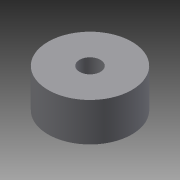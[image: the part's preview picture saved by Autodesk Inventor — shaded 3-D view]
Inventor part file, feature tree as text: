
AUTODESK INVENTOR PART (.ipt)
format: ipt  version: 2014 SP1 (Build 180222100, 222)  size: 84,480 bytes
history: native  units: in
note: dims shown in document units (in); Inventor stores cm internally (conversion verified against a paired STEP export)
features: extrude x2, sketch x2, hole x1
ambient origin geometry x8: Origin, YZ Plane, XZ Plane, XY Plane, X Axis, Y Axis, Z Axis, Center Point
bodies: Solid1 (feature_tree)
feature tree (5):
  extrude  "Extrusion1"  Depth=0.04in TaperAngle=0.0deg
  extrude  "Extrusion2"  Depth=0.46in TaperAngle=0.0deg
  hole  "Hole1"  [1 undecoded]
  sketch  "Sketch1"  dims[d0=0.75in d1=0.04in d2=0.0in]
  sketch  "Sketch2"  dims[d3=1.0in d4=0.46in d5=0.0in d6=1.0in d7=1.0in d8=0.25in d9=0.75in d10=0.375in d11=0.25in d12=0.5635in d13=1.0in d14=0.8108in]
note: 1 required parameter value undecoded (feature->parameter linkage not recoverable at this tier; creation-order binding heuristic only, values carry confidence <= 0.55)
